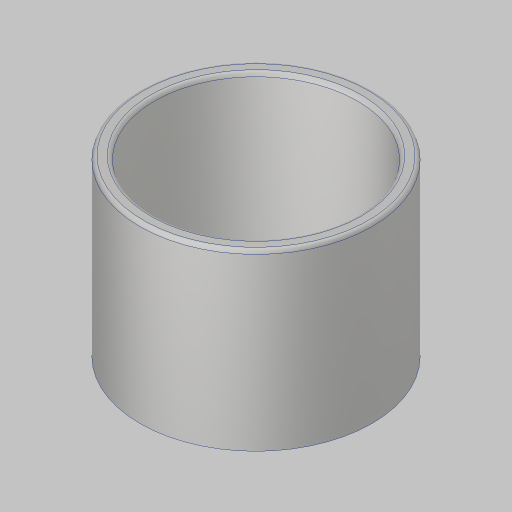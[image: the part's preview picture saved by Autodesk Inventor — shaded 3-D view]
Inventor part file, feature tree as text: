
AUTODESK INVENTOR PART (.ipt)
format: ipt  version: 2023.5 (Build 275446000, 446)  size: 151,552 bytes
history: native  units: in
note: dims shown in document units (in); Inventor stores cm internally (conversion verified against a paired STEP export)
features: extrude x2, sketch x2, fillet x1
ambient origin geometry x8: Origin, YZ Plane, XZ Plane, XY Plane, X Axis, Y Axis, Z Axis, Center Point
bodies: Solid1 (feature_tree)
feature tree (5):
  extrude  "Extrusion1"  Depth=1.5in TaperAngle=0.0deg
  extrude  "Extrusion4"  TaperAngle=0.0deg  [1 undecoded]
  fillet  "Fillet1"  Radius=0.0312in
  sketch  "Sketch1"  dims[d0=2.0in d1=1.5in d2=0.0in]
  sketch  "Sketch5"  dims[d32=1.75in d33=0.0in d34=0.0in d35=0.0312in]
note: 1 required parameter value undecoded (feature->parameter linkage not recoverable at this tier; creation-order binding heuristic only, values carry confidence <= 0.55)
